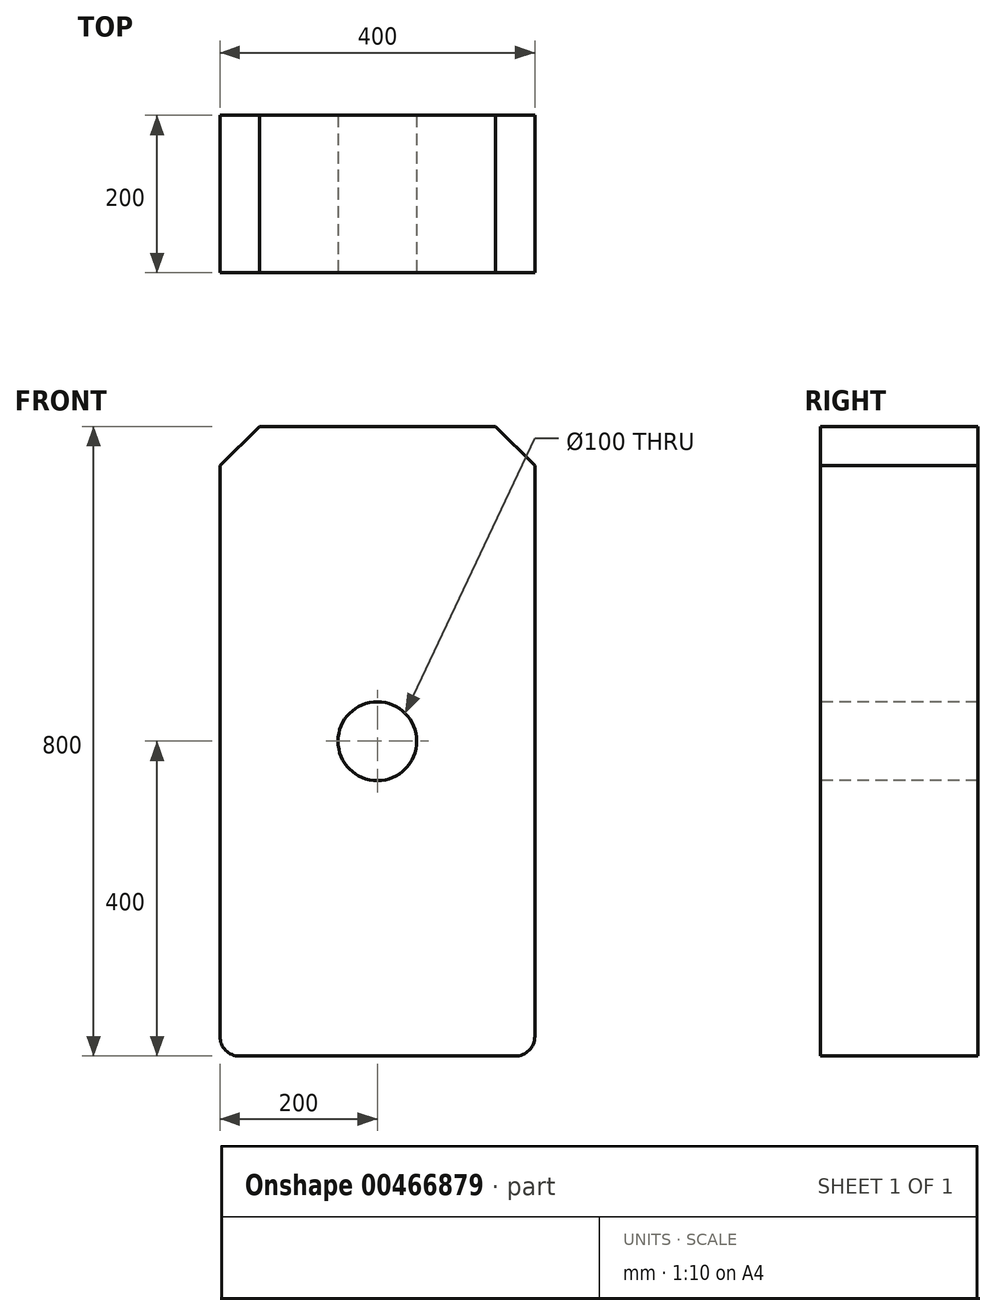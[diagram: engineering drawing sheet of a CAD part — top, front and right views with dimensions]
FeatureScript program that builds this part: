
annotation { "Feature Type Name" : "Feature", "Feature Type Description" : "" }
export const myFeature = defineFeature(function(context is Context, id is Id, definition is map)
    precondition{}
    {
        {
            var Q0;
            Q0=qCreatedBy(makeId("Front.planeOp"),FACE);
            var sketch = newSketch(context, id + "F0", { "sketchPlane" : qUnion([Q0])});
            skLineSegment(sketch, "E0.bottom", {"start": v(-200, -400) * mm, "end": v(200, -400) * mm});
            skLineSegment(sketch, "E0.top", {"start": v(-200, 400) * mm, "end": v(200, 400) * mm});
            skLineSegment(sketch, "E0.left", {"start": v(-200, -400) * mm, "end": v(-200, 400) * mm});
            skLineSegment(sketch, "E0.right", {"start": v(200, -400) * mm, "end": v(200, 400) * mm});
            skPoint(sketch, "E0.middle", {"position": v(0, 0) * mm});
            skSolve(sketch);
        }
        {
            var Q0;
            Q0 = qSketchRegion(id + "F0", true);
            extrude(context, id + "F1", {"entities" : qUnion([Q0]), "depth" : 200 * mm});
        }
        {
            var Q0;
            Q0=makeQuery(id+"F1.opExtrude","SWEPT_EDGE",EDGE,{"disambiguationData":[OSD([sQuery(id+"F0.wireOp",EDGE,"E0.top"),sQuery(id+"F0.wireOp",EDGE,"E0.left")])]});
            var Q1;
            Q1=makeQuery(id+"F1.opExtrude","SWEPT_EDGE",EDGE,{"disambiguationData":[OSD([sQuery(id+"F0.wireOp",EDGE,"E0.top"),sQuery(id+"F0.wireOp",EDGE,"E0.right")])]});
            chamfer(context, id + "F2", {"entities" : qUnion([Q0, Q1]), "width" : 50 * mm, "tangentPropagation" : true});
        }
        {
            var Q0;
            Q0=makeQuery(id+"F1.opExtrude","SWEPT_EDGE",EDGE,{"disambiguationData":[OSD([sQuery(id+"F0.wireOp",EDGE,"E0.bottom"),sQuery(id+"F0.wireOp",EDGE,"E0.left")])]});
            var Q1;
            Q1=makeQuery(id+"F1.opExtrude","SWEPT_EDGE",EDGE,{"disambiguationData":[OSD([sQuery(id+"F0.wireOp",EDGE,"E0.bottom"),sQuery(id+"F0.wireOp",EDGE,"E0.right")])]});
            fillet(context, id + "F3", {"entities" : qUnion([Q0, Q1]), "radius" : 25 * mm, "tangentPropagation" : true, "allowEdgeOverflow" : false});
        }
        {
            var Q0;
            Q0=makeQuery(id+"F1.opExtrude","CAP_FACE",FACE,{"disambiguationData":[OSD([sQuery(id+"F0.wireOp",EDGE,"E0.bottom"),sQuery(id+"F0.wireOp",EDGE,"E0.top"),sQuery(id+"F0.wireOp",EDGE,"E0.left"),sQuery(id+"F0.wireOp",EDGE,"E0.right")])],"isStart":false});
            var sketch = newSketch(context, id + "F4", { "sketchPlane" : qUnion([Q0])});
            skCircle(sketch, "E1", {"center": v(0, 0) * mm, "radius": 50 * mm});
            skSolve(sketch);
        }
        {
            var Q0;
            Q0 = qSketchRegion(id + "F4", true);
            extrude(context, id + "F5", {"entities" : qUnion([Q0]), "operationType" : NewBodyOperationType.REMOVE, "endBound" : BoundingType.THROUGH_ALL, "oppositeDirection" : true, "depth" : 25 * mm});
        }
    });
